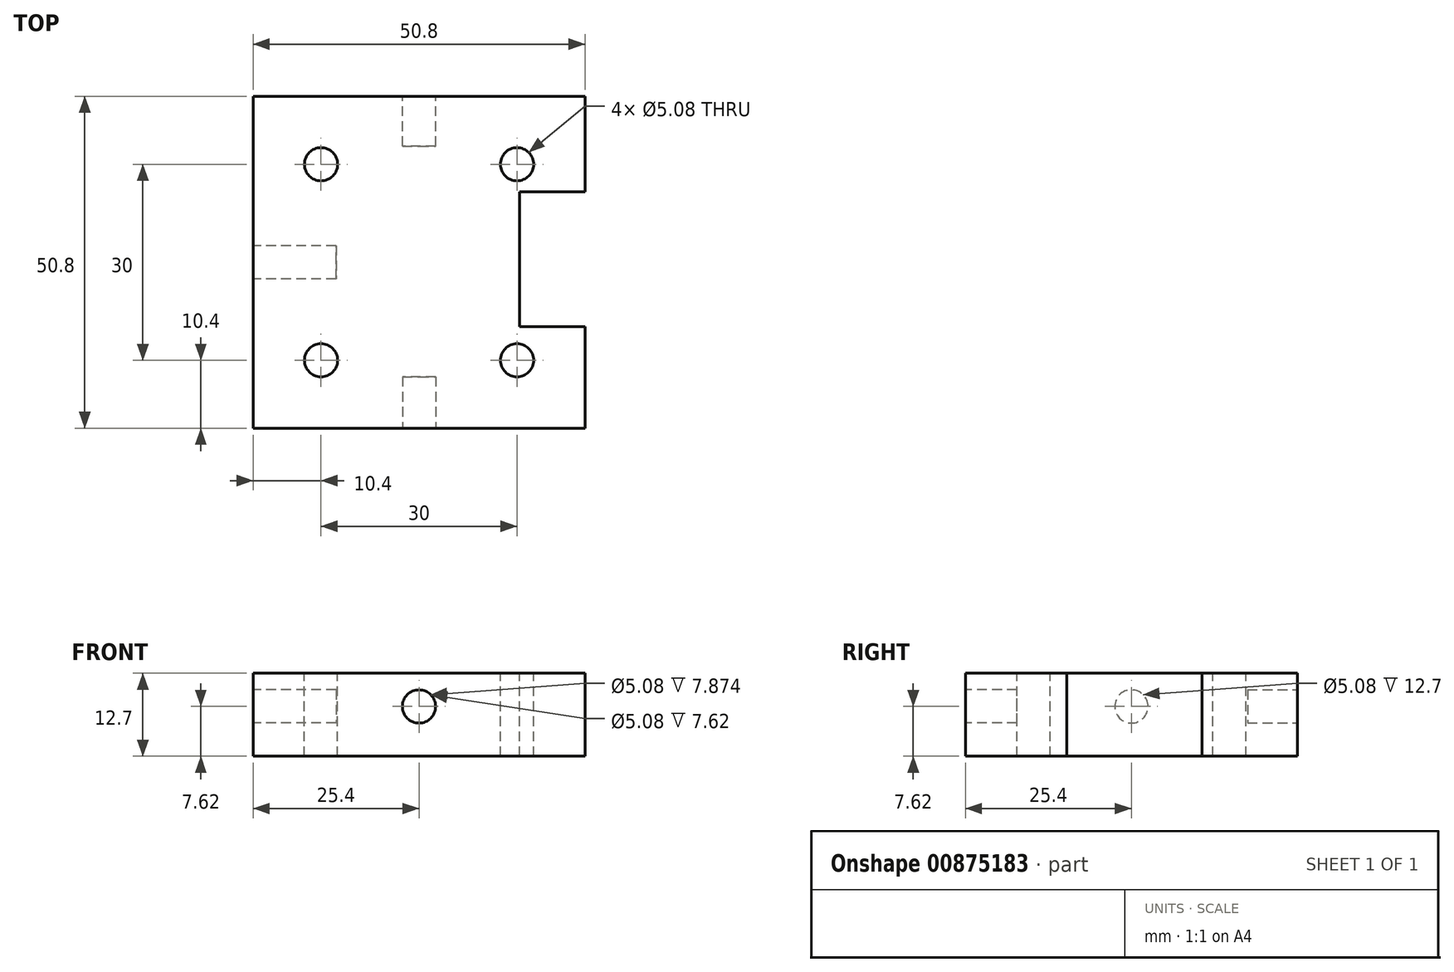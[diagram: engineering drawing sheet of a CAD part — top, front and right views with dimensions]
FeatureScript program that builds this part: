
annotation { "Feature Type Name" : "Feature", "Feature Type Description" : "" }
export const myFeature = defineFeature(function(context is Context, id is Id, definition is map)
    precondition{}
    {
        {
            var Q0;
            Q0=qCreatedBy(makeId("Top.planeOp"),FACE);
            var sketch = newSketch(context, id + "F0", { "sketchPlane" : qUnion([Q0])});
            skLineSegment(sketch, "E0.bottom", {"start": v(-25.4, 25.4) * mm, "end": v(25.4, 25.4) * mm});
            skLineSegment(sketch, "E0.top", {"start": v(-25.4, -25.4) * mm, "end": v(25.4, -25.4) * mm});
            skLineSegment(sketch, "E0.left", {"start": v(-25.4, 25.4) * mm, "end": v(-25.4, -25.4) * mm});
            skLineSegment(sketch, "E0.right", {"start": v(25.4, 25.4) * mm, "end": v(25.4, -25.4) * mm});
            skPoint(sketch, "E0.middle", {"position": v(0, 0) * mm});
            skSolve(sketch);
        }
        {
            var Q0;
            Q0=makeQuery(id+"F0.imprint","IMPRINT",FACE,{"disambiguationData":[TD([[makeQuery(id+"F0.imprint","IMPRINT",EDGE,{"derivedFrom":sQuery(id+"F0.wireOp",EDGE,"E0.bottom")}),-1.0]])]});
            extrude(context, id + "F1", {"entities" : qUnion([Q0]), "depth" : 12.7 * mm, "offsetDistance" : 25.4 * mm});
        }
        {
            var Q0;
            Q0=makeQuery(id+"F1.opExtrude","CAP_FACE",FACE,{"disambiguationData":[OSD([sQuery(id+"F0.wireOp",EDGE,"E0.bottom"),sQuery(id+"F0.wireOp",EDGE,"E0.top"),sQuery(id+"F0.wireOp",EDGE,"E0.left"),sQuery(id+"F0.wireOp",EDGE,"E0.right")])],"isStart":false});
            var sketch = newSketch(context, id + "F2", { "sketchPlane" : qUnion([Q0])});
            skLineSegment(sketch, "E1.bottom", {"start": v(25.4, -9.88) * mm, "end": v(15.4, -9.88) * mm});
            skLineSegment(sketch, "E1.top", {"start": v(25.4, 10.8) * mm, "end": v(15.4, 10.8) * mm});
            skLineSegment(sketch, "E1.left", {"start": v(25.4, -9.88) * mm, "end": v(25.4, 10.8) * mm});
            skLineSegment(sketch, "E1.right", {"start": v(15.4, -9.88) * mm, "end": v(15.4, 10.8) * mm});
            skPoint(sketch, "E1.middle", {"position": v(20.4, 0.46) * mm});
            skSolve(sketch);
        }
        {
            var Q0;
            Q0 = qSketchRegion(id + "F2", true);
            extrude(context, id + "F3", {"entities" : qUnion([Q0]), "operationType" : NewBodyOperationType.REMOVE, "oppositeDirection" : true, "depth" : 25.4 * mm, "offsetDistance" : 25.4 * mm});
        }
        {
            var Q0;
            Q0=makeQuery(id+"F1.opExtrude","CAP_FACE",FACE,{"disambiguationData":[OSD([sQuery(id+"F0.wireOp",EDGE,"E0.bottom"),sQuery(id+"F0.wireOp",EDGE,"E0.top"),sQuery(id+"F0.wireOp",EDGE,"E0.left"),sQuery(id+"F0.wireOp",EDGE,"E0.right")])],"isStart":false});
            var sketch = newSketch(context, id + "F4", { "sketchPlane" : qUnion([Q0])});
            skPoint(sketch, "E2.middle", {"position": v(0, 0) * mm});
            skCircle(sketch, "E3", {"center": v(-15, 15) * mm, "radius": 2.54 * mm});
            skCircle(sketch, "E4", {"center": v(15, 15) * mm, "radius": 2.54 * mm});
            skCircle(sketch, "E5", {"center": v(-15, -15) * mm, "radius": 2.54 * mm});
            skCircle(sketch, "E6", {"center": v(15, -15) * mm, "radius": 2.54 * mm});
            skSolve(sketch);
        }
        {
            var Q0;
            Q0 = qSketchRegion(id + "F4", true);
            var Q1;
            Q1 = qConstructionFilter(qBodyType(qCreatedBy(id + "F4" ,EDGE), BodyType.WIRE), ConstructionObject.NO);
            extrude(context, id + "F5", {"entities" : qUnion([Q0]), "operationType" : NewBodyOperationType.REMOVE, "surfaceEntities" : qUnion([Q1]), "oppositeDirection" : true, "depth" : 25.4 * mm, "offsetDistance" : 25.4 * mm});
        }
        {
            var Q0;
            Q0=makeQuery(id+"F1.opExtrude","SWEPT_FACE",FACE,{"disambiguationData":[OSD([sQuery(id+"F0.wireOp",EDGE,"E0.top")])]});
            var sketch = newSketch(context, id + "F6", { "sketchPlane" : qUnion([Q0])});
            skCircle(sketch, "E7", {"center": v(0, 7.62) * mm, "radius": 2.54 * mm});
            skSolve(sketch);
        }
        {
            var Q0;
            Q0=makeQuery(id+"F6.imprint","IMPRINT",FACE,{"disambiguationData":[TD([[makeQuery(id+"F6.imprint","IMPRINT",EDGE,{"derivedFrom":sQuery(id+"F6.wireOp",EDGE,"E7")}),1.0]])]});
            var Q1;
            Q1=sQuery(id+"F6.wireOp",EDGE,"E7");
            extrude(context, id + "F7", {"entities" : qUnion([Q0]), "operationType" : NewBodyOperationType.REMOVE, "surfaceEntities" : qUnion([Q1]), "oppositeDirection" : true, "depth" : 7.87 * mm, "offsetDistance" : 25.4 * mm});
        }
        {
            var Q0;
            Q0=makeQuery(id+"F1.opExtrude","SWEPT_FACE",FACE,{"disambiguationData":[OSD([sQuery(id+"F0.wireOp",EDGE,"E0.left")])]});
            var sketch = newSketch(context, id + "F8", { "sketchPlane" : qUnion([Q0])});
            skCircle(sketch, "E8", {"center": v(0, 7.62) * mm, "radius": 2.54 * mm});
            skSolve(sketch);
        }
        {
            var Q0;
            Q0=makeQuery(id+"F8.imprint","IMPRINT",FACE,{"disambiguationData":[TD([[makeQuery(id+"F8.imprint","IMPRINT",EDGE,{"derivedFrom":sQuery(id+"F8.wireOp",EDGE,"E8")}),1.0]])]});
            var Q1;
            Q1=sQuery(id+"F8.wireOp",EDGE,"E8");
            extrude(context, id + "F9", {"entities" : qUnion([Q0]), "operationType" : NewBodyOperationType.REMOVE, "surfaceEntities" : qUnion([Q1]), "oppositeDirection" : true, "depth" : 12.7 * mm, "offsetDistance" : 25.4 * mm});
        }
        {
            var Q0;
            Q0=makeQuery(id+"F1.opExtrude","SWEPT_FACE",FACE,{"disambiguationData":[OSD([sQuery(id+"F0.wireOp",EDGE,"E0.bottom")])]});
            var sketch = newSketch(context, id + "F10", { "sketchPlane" : qUnion([Q0])});
            skCircle(sketch, "E9", {"center": v(0, 7.62) * mm, "radius": 2.54 * mm});
            skPoint(sketch, "E9.centerSnap0", {"position": v(0, 0) * mm});
            skSolve(sketch);
        }
        {
            var Q0;
            Q0=makeQuery(id+"F10.imprint","IMPRINT",FACE,{"disambiguationData":[TD([[makeQuery(id+"F10.imprint","IMPRINT",EDGE,{"derivedFrom":sQuery(id+"F10.wireOp",EDGE,"E9")}),1.0]])]});
            var Q1;
            Q1=sQuery(id+"F10.wireOp",EDGE,"E9");
            extrude(context, id + "F11", {"entities" : qUnion([Q0]), "operationType" : NewBodyOperationType.REMOVE, "surfaceEntities" : qUnion([Q1]), "oppositeDirection" : true, "depth" : 7.62 * mm, "offsetDistance" : 25.4 * mm});
        }
    });
